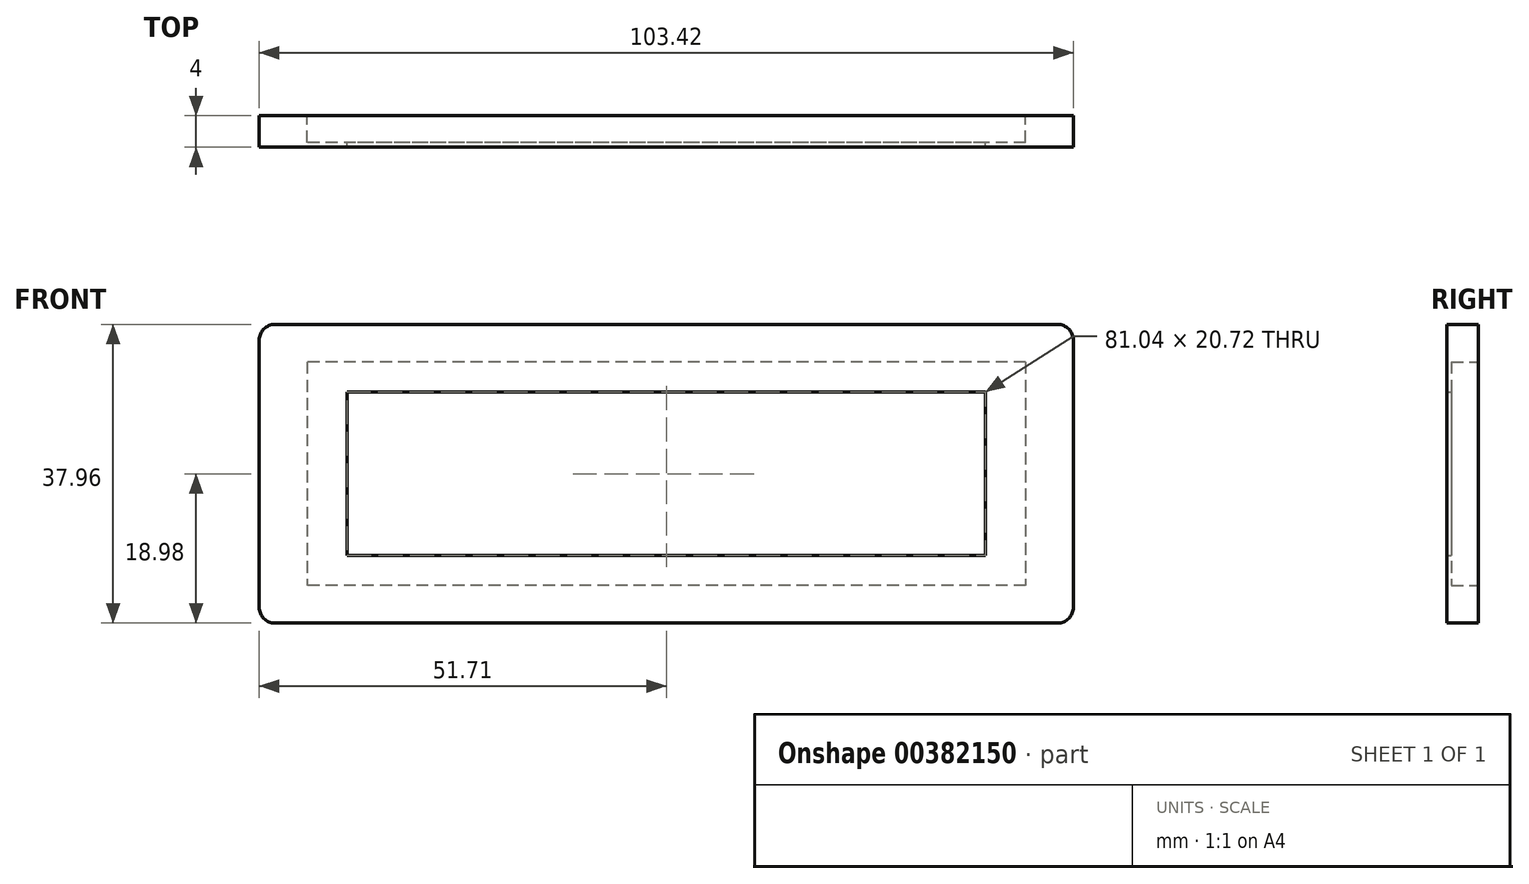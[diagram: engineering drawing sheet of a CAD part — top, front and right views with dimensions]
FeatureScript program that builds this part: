
annotation { "Feature Type Name" : "Feature", "Feature Type Description" : "" }
export const myFeature = defineFeature(function(context is Context, id is Id, definition is map)
    precondition{}
    {
        {
            var Q0;
            Q0=qCreatedBy(makeId("Front.planeOp"),FACE);
            var sketch = newSketch(context, id + "F0", { "sketchPlane" : qUnion([Q0])});
            skLineSegment(sketch, "E0.bottom", {"start": v(51.7, 18.98) * mm, "end": v(-51.7, 18.98) * mm});
            skLineSegment(sketch, "E0.top", {"start": v(51.7, -18.98) * mm, "end": v(-51.7, -18.98) * mm});
            skLineSegment(sketch, "E0.left", {"start": v(51.7, 18.98) * mm, "end": v(51.7, -18.98) * mm});
            skLineSegment(sketch, "E0.right", {"start": v(-51.7, 18.98) * mm, "end": v(-51.7, -18.98) * mm});
            skPoint(sketch, "E0.middle", {"position": v(0, 0) * mm});
            skLineSegment(sketch, "E1.bottom", {"start": v(40.52, 10.36) * mm, "end": v(-40.52, 10.36) * mm});
            skLineSegment(sketch, "E1.top", {"start": v(40.52, -10.36) * mm, "end": v(-40.52, -10.36) * mm});
            skLineSegment(sketch, "E1.left", {"start": v(40.52, 10.36) * mm, "end": v(40.52, -10.36) * mm});
            skLineSegment(sketch, "E1.right", {"start": v(-40.52, 10.36) * mm, "end": v(-40.52, -10.36) * mm});
            skSolve(sketch);
        }
        {
            var Q0;
            Q0=makeQuery(id+"F0.imprint","IMPRINT",FACE,{"disambiguationData":[TD([[makeQuery(id+"F0.imprint","IMPRINT",EDGE,{"derivedFrom":sQuery(id+"F0.wireOp",EDGE,"E0.bottom")}),1.0]])]});
            extrude(context, id + "F1", {"entities" : qUnion([Q0]), "depth" : 4 * mm});
        }
        {
            var Q0;
            Q0=makeQuery(id+"F1.opExtrude","CAP_FACE",FACE,{"disambiguationData":[OSD([sQuery(id+"F0.wireOp",EDGE,"E0.bottom"),sQuery(id+"F0.wireOp",EDGE,"E0.top"),sQuery(id+"F0.wireOp",EDGE,"E0.left"),sQuery(id+"F0.wireOp",EDGE,"E0.right"),sQuery(id+"F0.wireOp",EDGE,"E1.bottom"),sQuery(id+"F0.wireOp",EDGE,"E1.top"),sQuery(id+"F0.wireOp",EDGE,"E1.left"),sQuery(id+"F0.wireOp",EDGE,"E1.right")])],"isStart":true});
            var sketch = newSketch(context, id + "F2", { "sketchPlane" : qUnion([Q0])});
            skLineSegment(sketch, "E2.bottom", {"start": v(-45.65, 14.2) * mm, "end": v(45.65, 14.2) * mm});
            skLineSegment(sketch, "E2.top", {"start": v(-45.65, -14.2) * mm, "end": v(45.65, -14.2) * mm});
            skLineSegment(sketch, "E2.left", {"start": v(-45.65, 14.2) * mm, "end": v(-45.65, -14.2) * mm});
            skLineSegment(sketch, "E2.right", {"start": v(45.65, 14.2) * mm, "end": v(45.65, -14.2) * mm});
            skPoint(sketch, "E2.middle", {"position": v(0, 0) * mm});
            skSolve(sketch);
        }
        {
            var Q0;
            Q0=makeQuery(id+"F2.imprint","IMPRINT",FACE,{"disambiguationData":[TD([[makeQuery(id+"F2.imprint","IMPRINT",EDGE,{"derivedFrom":sQuery(id+"F2.wireOp",EDGE,"E2.bottom")}),-1.0]])]});
            extrude(context, id + "F3", {"entities" : qUnion([Q0]), "operationType" : NewBodyOperationType.REMOVE, "oppositeDirection" : true, "depth" : 3.4 * mm});
        }
        {
            var Q0;
            Q0=makeQuery(id+"F1.opExtrude","SWEPT_EDGE",EDGE,{"disambiguationData":[OSD([sQuery(id+"F0.wireOp",EDGE,"E0.bottom"),sQuery(id+"F0.wireOp",EDGE,"E0.right")])]});
            var Q1;
            Q1=makeQuery(id+"F1.opExtrude","SWEPT_EDGE",EDGE,{"disambiguationData":[OSD([sQuery(id+"F0.wireOp",EDGE,"E0.bottom"),sQuery(id+"F0.wireOp",EDGE,"E0.left")])]});
            var Q2;
            Q2=makeQuery(id+"F1.opExtrude","SWEPT_EDGE",EDGE,{"disambiguationData":[OSD([sQuery(id+"F0.wireOp",EDGE,"E0.top"),sQuery(id+"F0.wireOp",EDGE,"E0.left")])]});
            var Q3;
            Q3=makeQuery(id+"F1.opExtrude","SWEPT_EDGE",EDGE,{"disambiguationData":[OSD([sQuery(id+"F0.wireOp",EDGE,"E0.top"),sQuery(id+"F0.wireOp",EDGE,"E0.right")])]});
            fillet(context, id + "F4", {"entities" : qUnion([Q0, Q1, Q2, Q3]), "radius" : 2 * mm, "tangentPropagation" : true, "allowEdgeOverflow" : false});
        }
    });
